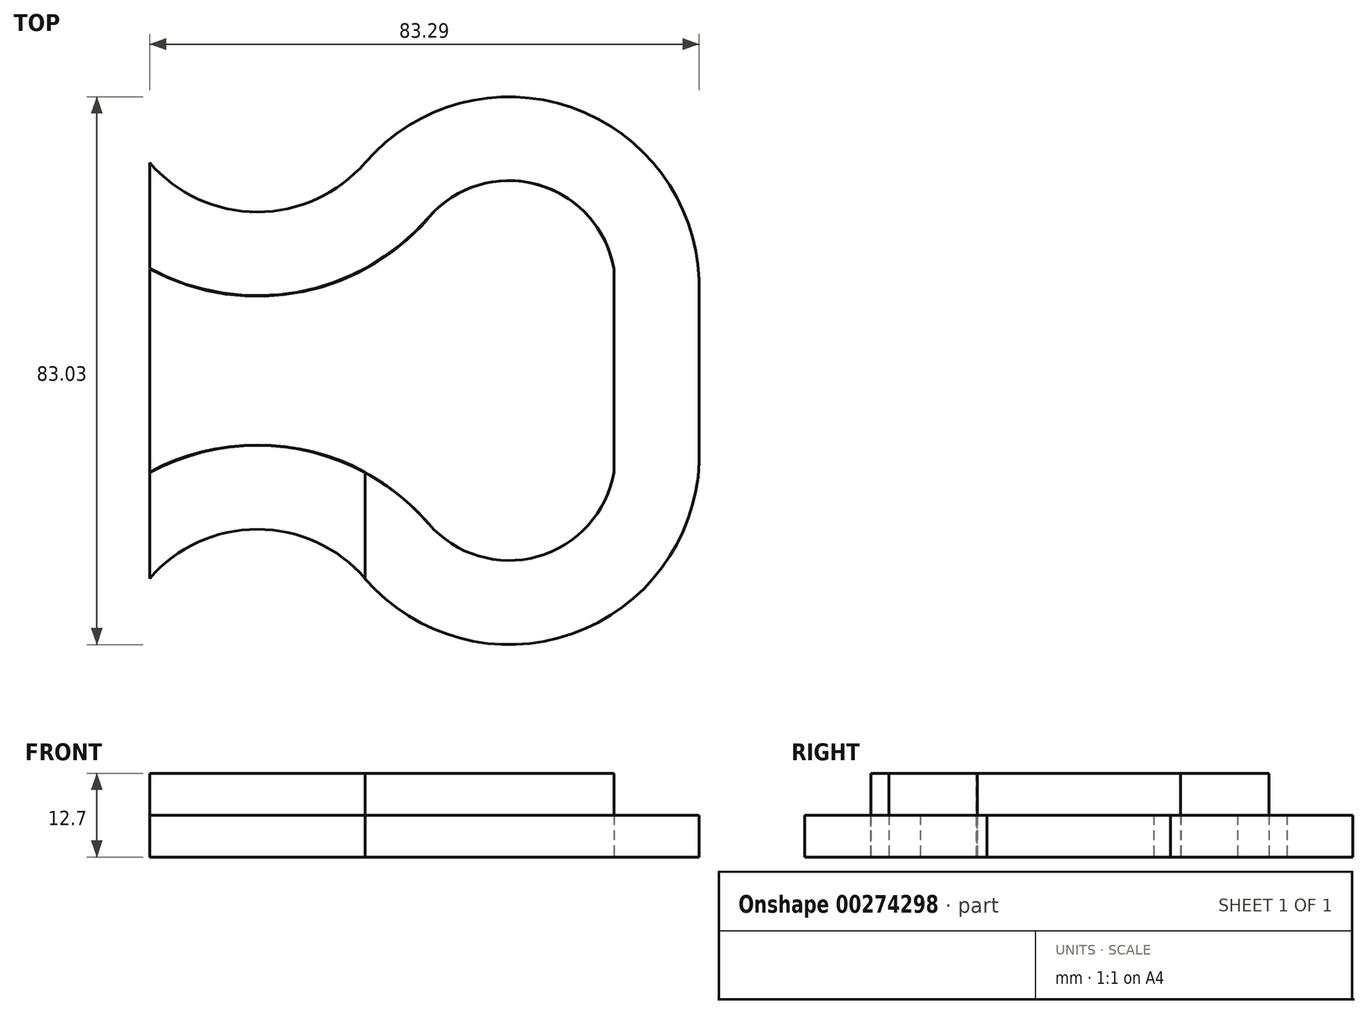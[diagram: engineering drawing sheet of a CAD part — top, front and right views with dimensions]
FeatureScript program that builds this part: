
annotation { "Feature Type Name" : "Feature", "Feature Type Description" : "" }
export const myFeature = defineFeature(function(context is Context, id is Id, definition is map)
    precondition{}
    {
        {
            var Q0;
            Q0=qCreatedBy(makeId("Top.planeOp"),FACE);
            var sketch = newSketch(context, id + "F0", { "sketchPlane" : qUnion([Q0])});
            skArc(sketch, "E0", {"start": v(-65.98, -27.39) * mm, "mid": v(-45.7, 1.9) * mm, "end": v(-11.74, -8.83) * mm});
            skArc(sketch, "E1.0", {"start": v(-53.29, -27) * mm, "mid": v(-41.59, -10.12) * mm, "end": v(-22, -16.31) * mm});
            skArc(sketch, "E2", {"start": v(-11.74, -8.83) * mm, "mid": v(4.6, -16.3) * mm, "end": v(20.92, -8.83) * mm});
            skArc(sketch, "E3.0", {"start": v(-21.35, -17.13) * mm, "mid": v(4.6, -29) * mm, "end": v(30.53, -17.13) * mm});
            skArc(sketch, "E4", {"start": v(71.53, -26.5) * mm, "mid": v(52.22, -0.47) * mm, "end": v(20.92, -8.83) * mm});
            skArc(sketch, "E5.0", {"start": v(58.62, -24.96) * mm, "mid": v(47.05, -12.15) * mm, "end": v(30.53, -17.13) * mm});
            skArc(sketch, "E6.MirrorCS", {"start": v(-53.29, -53.69) * mm, "mid": v(-41.59, -70.58) * mm, "end": v(-22, -64.38) * mm});
            skArc(sketch, "E7.MirrorCS", {"start": v(-21.35, -63.56) * mm, "mid": v(4.6, -51.7) * mm, "end": v(30.53, -63.56) * mm});
            skArc(sketch, "E8.MirrorCS", {"start": v(58.62, -55.73) * mm, "mid": v(47.05, -68.55) * mm, "end": v(30.53, -63.56) * mm});
            skArc(sketch, "E9.MirrorCS", {"start": v(71.55, -54.26) * mm, "mid": v(52.24, -80.28) * mm, "end": v(20.94, -71.92) * mm});
            skArc(sketch, "E10.MirrorCS", {"start": v(-65.98, -53.3) * mm, "mid": v(-45.7, -82.6) * mm, "end": v(-11.74, -71.87) * mm});
            skArc(sketch, "E11.MirrorCS", {"start": v(-11.74, -71.87) * mm, "mid": v(4.6, -64.4) * mm, "end": v(20.92, -71.87) * mm});
            skFitSpline(sketch, "E12", {"points": [v(-65.98, -27.39) * mm, v(-65.98, -53.3) * mm], "startDerivative": vector(0, -25.92) * mm, "endDerivative": vector(0, -25.92) * mm});
            skFitSpline(sketch, "E13", {"points": [v(71.53, -26.5) * mm, v(71.55, -54.26) * mm], "startDerivative": vector(0, -27.71) * mm, "endDerivative": vector(0, -27.71) * mm});
            skFitSpline(sketch, "E14", {"points": [v(58.62, -24.96) * mm, v(58.62, -55.73) * mm], "startDerivative": vector(0, -30.77) * mm, "endDerivative": vector(0, -30.77) * mm});
            skFitSpline(sketch, "E15", {"points": [v(-53.29, -53.69) * mm, v(-53.29, -27) * mm], "startDerivative": vector(0, 26.68) * mm, "endDerivative": vector(0, 26.68) * mm});
            skArc(sketch, "E16", {"start": v(-21.35, -63.56) * mm, "mid": v(4.61, -51.7) * mm, "end": v(30.56, -63.6) * mm});
            skLineSegment(sketch, "E17", {"start": v(-11.74, -8.83) * mm, "end": v(-11.74, -71.87) * mm});
            skLineSegment(sketch, "E18", {"start": v(20.92, -8.83) * mm, "end": v(20.94, -71.92) * mm});
            skArc(sketch, "E19", {"start": v(-11.74, -71.87) * mm, "mid": v(4.6, -64.4) * mm, "end": v(20.94, -71.89) * mm});
            skArc(sketch, "E20", {"start": v(-53.29, -27) * mm, "mid": v(-41.03, -9.94) * mm, "end": v(-21.35, -17.28) * mm});
            skArc(sketch, "E21", {"start": v(-53.29, -53.69) * mm, "mid": v(-41.03, -70.76) * mm, "end": v(-21.35, -63.42) * mm});
            skArc(sketch, "E22", {"start": v(-21.35, -17.28) * mm, "mid": v(5.36, -29.08) * mm, "end": v(31.51, -16.1) * mm});
            skArc(sketch, "E23", {"start": v(-21.35, -63.42) * mm, "mid": v(4.69, -51.6) * mm, "end": v(30.65, -63.56) * mm});
            skFitSpline(sketch, "E24", {"points": [v(-53.29, -27) * mm, v(-53.29, -53.69) * mm], "startDerivative": vector(0, -26.68) * mm, "endDerivative": vector(0, -26.68) * mm});
            skSolve(sketch);
        }
        {
            var Q0;
            {var subQ7=sQuery(id+"F0.wireOp",EDGE,"E0");Q0=makeQuery(id+"F0.imprint","IMPRINT",FACE,{"disambiguationData":[TD([[makeQuery(id+"F0.imprint","IMPRINT",EDGE,{"derivedFrom":subQ7}),-1.0]])]});}
            var Q1;
            {var subQ5=sQuery(id+"F0.wireOp",EDGE,"E2");Q1=makeQuery(id+"F0.imprint","IMPRINT",FACE,{"disambiguationData":[TD([[makeQuery(id+"F0.imprint","IMPRINT",EDGE,{"derivedFrom":subQ5}),-1.0]])]});}
            var Q2;
            {var subQ8=sQuery(id+"F0.wireOp",EDGE,"E4");Q2=makeQuery(id+"F0.imprint","IMPRINT",FACE,{"disambiguationData":[TD([[makeQuery(id+"F0.imprint","IMPRINT",EDGE,{"derivedFrom":subQ8}),1.0]])]});}
            var Q3;
            {var subQ2=sQuery(id+"F0.wireOp",EDGE,"E11.MirrorCS");Q3=makeQuery(id+"F0.imprint","IMPRINT",FACE,{"disambiguationData":[TD([[makeQuery(id+"F0.imprint","IMPRINT",EDGE,{"derivedFrom":subQ2}),1.0]])]});}
            extrude(context, id + "F1", {"entities" : qUnion([Q0, Q1, Q2, Q3]), "depth" : 6.35 * mm});
        }
        {
            var Q0;
            {var subQ0=sQuery(id+"F0.wireOp",EDGE,"E11.MirrorCS");Q0=makeQuery(id+"F0.imprint","IMPRINT",FACE,{"disambiguationData":[TD([[makeQuery(id+"F0.imprint","IMPRINT",EDGE,{"derivedFrom":subQ0}),-1.0]])]});}
            var Q1;
            {var subQ0=sQuery(id+"F0.wireOp",EDGE,"E24");Q1=makeQuery(id+"F0.imprint","IMPRINT",FACE,{"disambiguationData":[TD([[makeQuery(id+"F0.imprint","IMPRINT",EDGE,{"derivedFrom":subQ0}),1.0]])]});}
            var Q2;
            {var subQ0=sQuery(id+"F0.wireOp",EDGE,"E14");Q2=makeQuery(id+"F0.imprint","IMPRINT",FACE,{"disambiguationData":[TD([[makeQuery(id+"F0.imprint","IMPRINT",EDGE,{"derivedFrom":subQ0}),-1.0]])]});}
            var Q3;
            {var subQ0=sQuery(id+"F0.wireOp",EDGE,"E22");var subQ1=sQuery(id+"F0.wireOp",EDGE,"E17");var subQ2=makeQuery(id+"F0.imprint","INTERSECT",VERTEX,{"derivedFrom":[subQ1,subQ0]});Q3=makeQuery(id+"F0.imprint","IMPRINT",FACE,{"disambiguationData":[TD([[makeQuery(id+"F0.imprint","IMPRINT",EDGE,{"disambiguationData":[TD([[subQ2,-1.0]])],"derivedFrom":subQ1}),1.0]])]});}
            extrude(context, id + "F2", {"entities" : qUnion([Q0, Q1, Q2, Q3]), "depth" : 12.7 * mm});
        }
    });
